# Revit family: rainselect_basic_set_for_3_functions_15311180___
name_source: partatom
category: Plumbing Fixtures
revit_build: Autodesk Revit 2015 (Build: 20140903_1530(x64)
units: mm (PartAtom-declared; Revit-internal decimal feet)

## types (1)
- n.a.
    BIMobject category = Installation Systems
    BOSUseNativeGeometries = 1
    Brand url = http://www.hansgrohe-int.com
    Default Elevation = 4' - 0"
    Design country = Germany
    EAN code = https://4059625034057
    Edition number = 1
    IFC Classification = Sanitary Terminal
    Installation instructions = https://pro.hansgrohe-int.com
    Manufacturer country = Germany
    Manufacturer name = hansgrohe
    Masterformat 2014 Code = 01 52 19
    Masterformat 2014 Description = Sanitary Facilities
    NBS Reference Code = 35-65-70-75
    NBS Reference Description = Sanitary Accessory Systems
    Nominal height = 0
    Nominal width = 0
    OmniClass Code = 23-19 31 17
    OmniClass Description = Sanitary Room Units
    Product Guid = 27e2e733-1542-46a4-b63e-ab2b433e4d73
    Product SKU = 15311180
    Product data url = https://bimobject.com
    Product family = RainSelect
    Product group = Concealed Basic set bath/shower mixers
    Product name = RainSelect Basic set for 3 functions 15311180
    Product url = https://pro.hansgrohe-int.com
    QR code = http://bimobject.com
    Technical description = https://pro.hansgrohe-int.com
    UNSPSC Code = 301815
    Uniclass 1.4 Code = L721
    Uniclass 1.4 Description = Sanitary equipment
    Uniclass 2.0 Code = SS-35-65-70-75
    Uniclass 2.0 Description = Sanitary Accessory Systems
    Uniclass 2015 Code = Pr_40_20
    Uniclass 2015 Name = Sanitary fittings and accessories
    Uniformat II Code = D2010
    Uniformat II Description = Plumbing Fixtures
    Weight Net (Kg) = 0

## geometry (parser evidence)
native form markers: Sweep x1
no freeform markers — native parametric forms only
